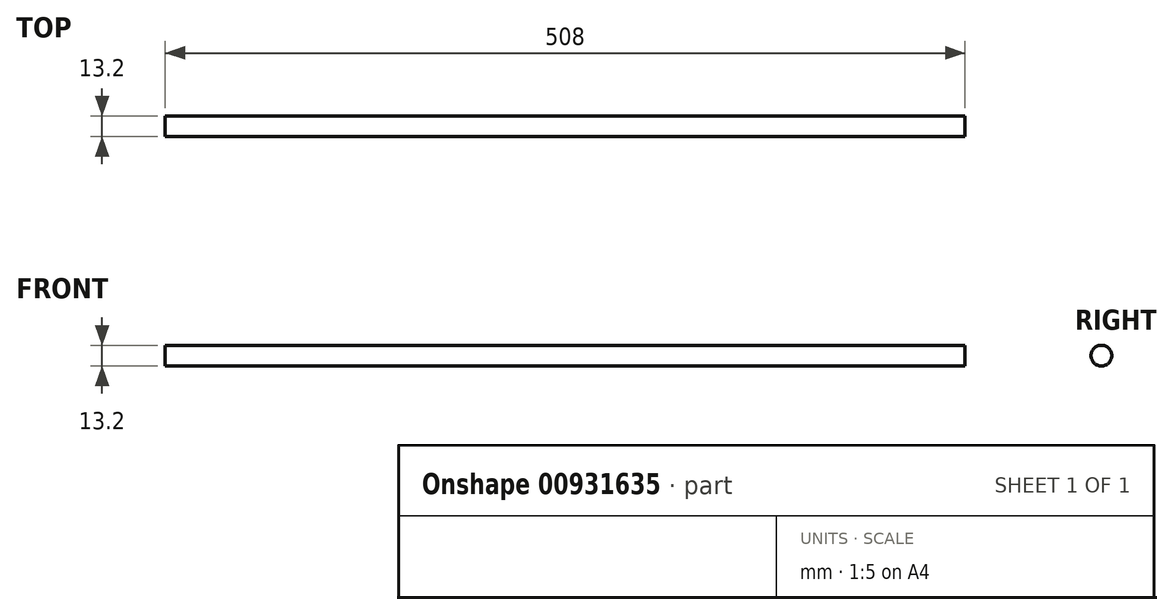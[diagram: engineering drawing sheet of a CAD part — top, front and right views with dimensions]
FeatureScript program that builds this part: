
annotation { "Feature Type Name" : "Feature", "Feature Type Description" : "" }
export const myFeature = defineFeature(function(context is Context, id is Id, definition is map)
    precondition{}
    {
        {
            var Q0;
            Q0=qCreatedBy(makeId("Right.planeOp"),FACE);
            var sketch = newSketch(context, id + "F0", { "sketchPlane" : qUnion([Q0])});
            skCircle(sketch, "E0", {"center": v(0, 0) * mm, "radius": 6.6 * mm});
            skSolve(sketch);
        }
        {
            var Q0;
            Q0=makeQuery(id+"F0.imprint","IMPRINT",FACE,{"disambiguationData":[TD([[makeQuery(id+"F0.imprint","IMPRINT",EDGE,{"derivedFrom":sQuery(id+"F0.wireOp",EDGE,"E0")}),1.0]])]});
            extrude(context, id + "F1", {"entities" : qUnion([Q0]), "depth" : 508 * mm, "offsetDistance" : 25.4 * mm});
        }
    });
